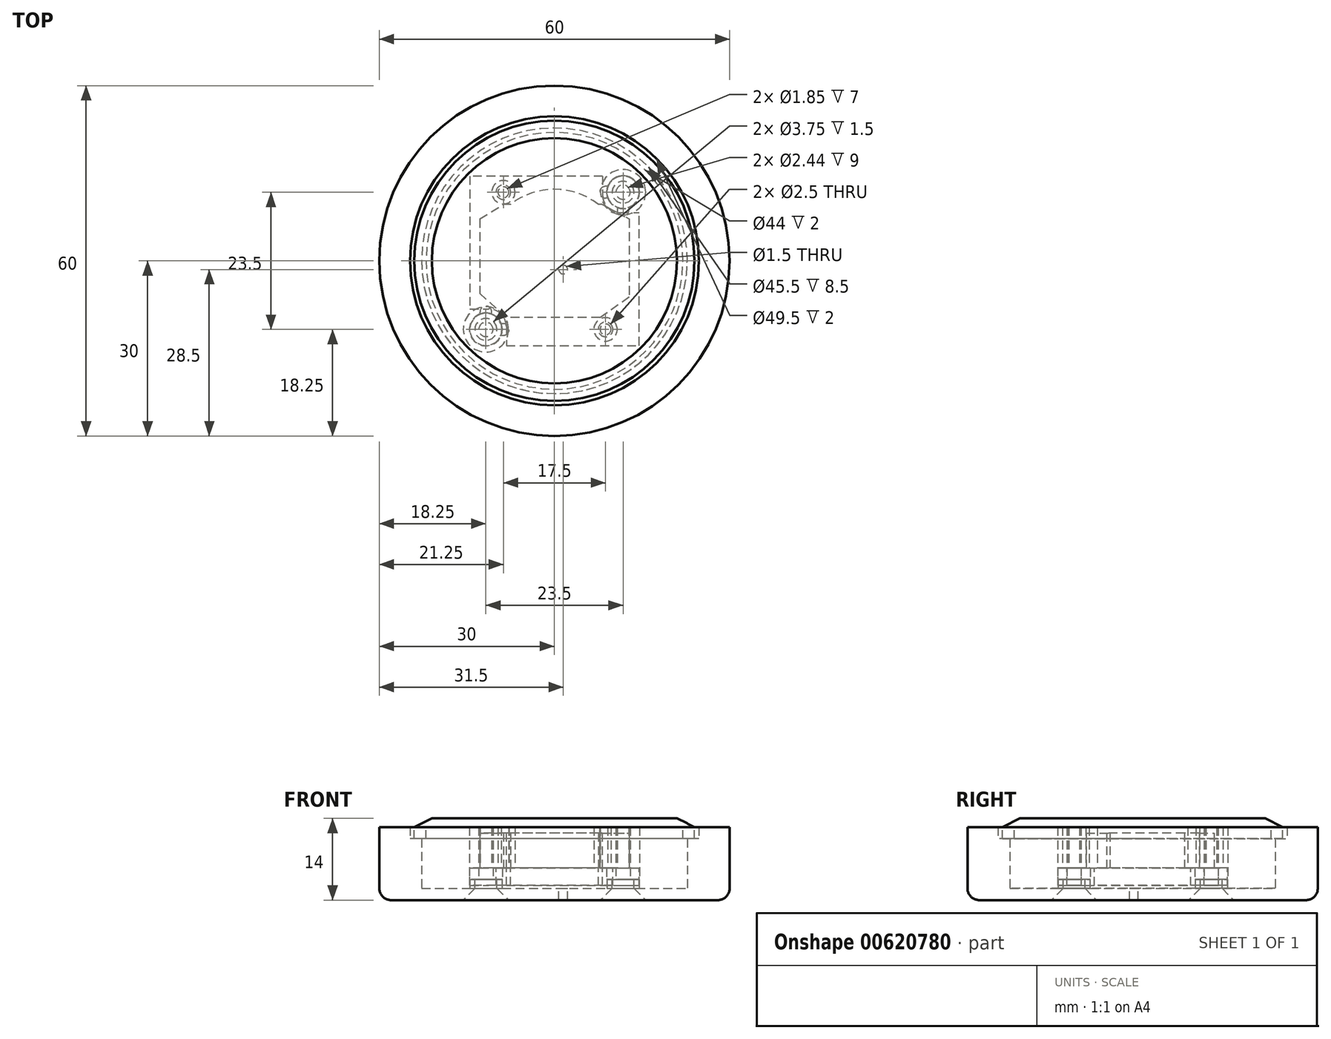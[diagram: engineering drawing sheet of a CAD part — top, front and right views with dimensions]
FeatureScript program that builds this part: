
annotation { "Feature Type Name" : "Feature", "Feature Type Description" : "" }
export const myFeature = defineFeature(function(context is Context, id is Id, definition is map)
    precondition{}
    {
        {
            var Q0;
            Q0=qCreatedBy(makeId("Top.planeOp"),FACE);
            var sketch = newSketch(context, id + "F0", { "sketchPlane" : qUnion([Q0])});
            skPoint(sketch, "E0.middle", {"position": v(0, 0) * mm});
            skCircle(sketch, "E1", {"center": v(-8.75, 11.75) * mm, "radius": 1.25 * mm});
            skLineSegment(sketch, "E2", {"start": v(8.25, 14.5) * mm, "end": v(8.25, 11.25) * mm});
            skLineSegment(sketch, "E3", {"start": v(11.25, 8.25) * mm, "end": v(14.5, 8.25) * mm});
            skLineSegment(sketch, "E4", {"start": v(8.25, 14.5) * mm, "end": v(-14.5, 14.5) * mm});
            skLineSegment(sketch, "E5", {"start": v(14.5, -14.5) * mm, "end": v(14.5, 8.25) * mm});
            skArc(sketch, "E6.filletArc", {"start": v(8.25, 11.25) * mm, "mid": v(9.13, 9.13) * mm, "end": v(11.25, 8.25) * mm});
            skLineSegment(sketch, "E7", {"start": v(-14.5, 14.5) * mm, "end": v(-14.5, -8.25) * mm});
            skLineSegment(sketch, "E8", {"start": v(-14.5, -8.25) * mm, "end": v(-11.25, -8.25) * mm});
            skLineSegment(sketch, "E9", {"start": v(-8.25, -11.25) * mm, "end": v(-8.25, -14.5) * mm});
            skLineSegment(sketch, "E10", {"start": v(-8.25, -14.5) * mm, "end": v(14.5, -14.5) * mm});
            skArc(sketch, "E11.filletArc", {"start": v(-8.25, -11.25) * mm, "mid": v(-9.13, -9.13) * mm, "end": v(-11.25, -8.25) * mm});
            skCircle(sketch, "E12", {"center": v(8.75, -11.75) * mm, "radius": 1.25 * mm});
            skSolve(sketch);
        }
        {
            var Q0;
            Q0=makeQuery(id+"F0.imprint","IMPRINT",FACE,{"disambiguationData":[TD([[makeQuery(id+"F0.imprint","IMPRINT",EDGE,{"derivedFrom":sQuery(id+"F0.wireOp",EDGE,"E1")}),-1.0]])]});
            extrude(context, id + "F1", {"entities" : qUnion([Q0]), "oppositeDirection" : true, "depth" : 3 * mm, "offsetDistance" : 25 * mm});
        }
        {
            var Q0;
            Q0=qCreatedBy(makeId("Top.planeOp"),FACE);
            var sketch = newSketch(context, id + "F2", { "sketchPlane" : qUnion([Q0])});
            skCircle(sketch, "E13", {"center": v(0, 0) * mm, "radius": 12.25 * mm});
            skLineSegment(sketch, "E14.bottom", {"start": v(12.8, 9.68) * mm, "end": v(-12.8, 9.68) * mm});
            skLineSegment(sketch, "E14.top", {"start": v(12.8, -9.68) * mm, "end": v(-12.8, -9.68) * mm});
            skLineSegment(sketch, "E14.left", {"start": v(12.8, 9.68) * mm, "end": v(12.8, -9.68) * mm});
            skLineSegment(sketch, "E14.right", {"start": v(-12.8, 9.68) * mm, "end": v(-12.8, -9.68) * mm});
            skLineSegment(sketch, "E15", {"start": v(8.17, 9.68) * mm, "end": v(12.8, 7.18) * mm});
            skLineSegment(sketch, "E16", {"start": v(7.8, -9.68) * mm, "end": v(12.8, -6.18) * mm});
            skLineSegment(sketch, "E17", {"start": v(-8.3, -9.68) * mm, "end": v(-12.8, -5.58) * mm});
            skLineSegment(sketch, "E18", {"start": v(-12.8, 7.18) * mm, "end": v(-8.71, 9.68) * mm});
            skSolve(sketch);
        }
        {
            var Q0;
            {var subQ0=sQuery(id+"F2.wireOp",EDGE,"E14.bottom");var subQ1=sQuery(id+"F2.wireOp",EDGE,"E13");var subQ2=makeQuery(id+"F2.imprint","INTERSECT",VERTEX,{"disambiguationData":[OD(0.0)],"derivedFrom":[subQ1,subQ0]});Q0=makeQuery(id+"F2.imprint","IMPRINT",FACE,{"disambiguationData":[TD([[makeQuery(id+"F2.imprint","IMPRINT",EDGE,{"disambiguationData":[TD([[subQ2,1.0]])],"derivedFrom":subQ1}),1.0]])]});}
            var Q1;
            {var subQ0=sQuery(id+"F2.wireOp",EDGE,"E14.top");var subQ1=sQuery(id+"F2.wireOp",EDGE,"E13");var subQ2=makeQuery(id+"F2.imprint","INTERSECT",VERTEX,{"disambiguationData":[OD(0.0)],"derivedFrom":[subQ1,subQ0]});Q1=makeQuery(id+"F2.imprint","IMPRINT",FACE,{"disambiguationData":[TD([[makeQuery(id+"F2.imprint","IMPRINT",EDGE,{"disambiguationData":[TD([[subQ2,-1.0]])],"derivedFrom":subQ1}),1.0]])]});}
            var Q2;
            {var subQ0=sQuery(id+"F2.wireOp",EDGE,"E17");Q2=makeQuery(id+"F2.imprint","IMPRINT",FACE,{"disambiguationData":[TD([[makeQuery(id+"F2.imprint","IMPRINT",EDGE,{"derivedFrom":subQ0}),-1.0]])]});}
            var Q3;
            {var subQ0=sQuery(id+"F2.wireOp",EDGE,"E15");Q3=makeQuery(id+"F2.imprint","IMPRINT",FACE,{"disambiguationData":[TD([[makeQuery(id+"F2.imprint","IMPRINT",EDGE,{"derivedFrom":subQ0}),-1.0]])]});}
            var Q4;
            {var subQ0=sQuery(id+"F2.wireOp",EDGE,"E14.bottom");var subQ1=sQuery(id+"F2.wireOp",EDGE,"E13");var subQ2=makeQuery(id+"F2.imprint","INTERSECT",VERTEX,{"disambiguationData":[OD(0.0)],"derivedFrom":[subQ1,subQ0]});Q4=makeQuery(id+"F2.imprint","IMPRINT",FACE,{"disambiguationData":[TD([[makeQuery(id+"F2.imprint","IMPRINT",EDGE,{"disambiguationData":[TD([[subQ2,-1.0]])],"derivedFrom":subQ1}),1.0]])]});}
            extrude(context, id + "F3", {"entities" : qUnion([Q0, Q1, Q2, Q3, Q4]), "operationType" : NewBodyOperationType.ADD, "depth" : 6 * mm, "offsetDistance" : 25 * mm});
        }
        {
            var Q0;
            Q0=qCreatedBy(makeId("Top.planeOp"),FACE);
            var sketch = newSketch(context, id + "F4", { "sketchPlane" : qUnion([Q0])});
            skCircle(sketch, "E19", {"center": v(-11.75, -11.75) * mm, "radius": 1.22 * mm});
            skCircle(sketch, "E20", {"center": v(11.75, 11.75) * mm, "radius": 1.22 * mm});
            skCircle(sketch, "E21", {"center": v(11.75, 11.75) * mm, "radius": 2.81 * mm});
            skCircle(sketch, "E22", {"center": v(-11.75, -11.75) * mm, "radius": 2.81 * mm});
            skLineSegment(sketch, "E23", {"start": v(-8.94, -8.94) * mm, "end": v(8.94, -8.94) * mm, "construction": true});
            skLineSegment(sketch, "E24", {"start": v(8.94, 8.94) * mm, "end": v(-8.94, 8.94) * mm, "construction": true});
            skLineSegment(sketch, "E25", {"start": v(8.94, -8.94) * mm, "end": v(8.94, 8.94) * mm, "construction": true});
            skLineSegment(sketch, "E26", {"start": v(-8.94, 8.94) * mm, "end": v(-8.94, -8.94) * mm, "construction": true});
            skPoint(sketch, "E27", {"position": v(-8.94, 0) * mm});
            skPoint(sketch, "E28", {"position": v(0, 8.94) * mm});
            skPoint(sketch, "E29", {"position": v(8.75, -11.75) * mm});
            skCircle(sketch, "E30", {"center": v(-8.75, 11.75) * mm, "radius": 2 * mm});
            skCircle(sketch, "E31", {"center": v(8.75, -11.75) * mm, "radius": 2 * mm});
            skCircle(sketch, "E32", {"center": v(-8.75, 11.75) * mm, "radius": 0.93 * mm});
            skCircle(sketch, "E33", {"center": v(8.75, -11.75) * mm, "radius": 0.93 * mm});
            skLineSegment(sketch, "E34", {"start": v(-11.75, -11.75) * mm, "end": v(-11.75, -7.75) * mm, "construction": true});
            skLineSegment(sketch, "E35", {"start": v(-8.94, 8.94) * mm, "end": v(8.94, -8.94) * mm, "construction": true});
            skLineSegment(sketch, "E36", {"start": v(-11.75, -7.75) * mm, "end": v(-11.75, -7.75) * mm});
            skLineSegment(sketch, "E37", {"start": v(-12.75, -9.12) * mm, "end": v(-12.75, -8.75) * mm});
            skPoint(sketch, "E38.visualSharp", {"position": v(-12.75, -7.75) * mm});
            skArc(sketch, "E38.filletArc", {"start": v(-11.75, -7.75) * mm, "mid": v(-12.46, -8.04) * mm, "end": v(-12.75, -8.75) * mm});
            skArc(sketch, "E39.MirrorCS", {"start": v(-11.75, -7.75) * mm, "mid": v(-11.04, -8.04) * mm, "end": v(-10.75, -8.75) * mm});
            skLineSegment(sketch, "E40.MirrorCS", {"start": v(-10.75, -9.12) * mm, "end": v(-10.75, -8.75) * mm});
            skLineSegment(sketch, "E41", {"start": v(8.94, 8.94) * mm, "end": v(-8.94, -8.94) * mm, "construction": true});
            skLineSegment(sketch, "E42.MirrorCS", {"start": v(-9.12, -12.75) * mm, "end": v(-8.75, -12.75) * mm});
            skArc(sketch, "E43.MirrorCS", {"start": v(-7.75, -11.75) * mm, "mid": v(-8.04, -12.46) * mm, "end": v(-8.75, -12.75) * mm});
            skArc(sketch, "E44.MirrorCS", {"start": v(-7.75, -11.75) * mm, "mid": v(-8.04, -11.04) * mm, "end": v(-8.75, -10.75) * mm});
            skLineSegment(sketch, "E45.MirrorCS", {"start": v(-9.12, -10.75) * mm, "end": v(-8.75, -10.75) * mm});
            skLineSegment(sketch, "E46.MirrorCS", {"start": v(10.75, 9.12) * mm, "end": v(10.75, 8.75) * mm});
            skArc(sketch, "E47.MirrorCS", {"start": v(11.75, 7.75) * mm, "mid": v(11.04, 8.04) * mm, "end": v(10.75, 8.75) * mm});
            skArc(sketch, "E48.MirrorCS", {"start": v(11.75, 7.75) * mm, "mid": v(12.46, 8.04) * mm, "end": v(12.75, 8.75) * mm});
            skLineSegment(sketch, "E49.MirrorCS", {"start": v(12.75, 9.12) * mm, "end": v(12.75, 8.75) * mm});
            skLineSegment(sketch, "E50.MirrorCS", {"start": v(9.12, 10.75) * mm, "end": v(8.75, 10.75) * mm});
            skArc(sketch, "E51.MirrorCS", {"start": v(7.75, 11.75) * mm, "mid": v(8.04, 11.04) * mm, "end": v(8.75, 10.75) * mm});
            skArc(sketch, "E52.MirrorCS", {"start": v(7.75, 11.75) * mm, "mid": v(8.04, 12.46) * mm, "end": v(8.75, 12.75) * mm});
            skLineSegment(sketch, "E53.MirrorCS", {"start": v(9.12, 12.75) * mm, "end": v(8.75, 12.75) * mm});
            skCircle(sketch, "E54", {"center": v(0, 0) * mm, "radius": 30 * mm, "construction": true});
            skCircle(sketch, "E55", {"center": v(1.5, -1.5) * mm, "radius": 0.75 * mm});
            skLineSegment(sketch, "E56", {"start": v(-11.75, -11.75) * mm, "end": v(1.5, -1.5) * mm, "construction": true});
            skLineSegment(sketch, "E57", {"start": v(-8.75, 11.75) * mm, "end": v(1.5, -1.5) * mm, "construction": true});
            skSolve(sketch);
        }
        {
            var Q0;
            Q0=makeQuery(id+"F4.imprint","IMPRINT",FACE,{"disambiguationData":[TD([[makeQuery(id+"F4.imprint","IMPRINT",EDGE,{"derivedFrom":sQuery(id+"F4.wireOp",EDGE,"E19")}),-1.0]])]});
            var Q1;
            Q1=makeQuery(id+"F4.imprint","IMPRINT",FACE,{"disambiguationData":[TD([[makeQuery(id+"F4.imprint","IMPRINT",EDGE,{"derivedFrom":sQuery(id+"F4.wireOp",EDGE,"E31")}),1.0]])]});
            var Q2;
            {var subQ0=sQuery(id+"F4.wireOp",EDGE,"E42.MirrorCS");Q2=makeQuery(id+"F4.imprint","IMPRINT",FACE,{"disambiguationData":[TD([[makeQuery(id+"F4.imprint","IMPRINT",EDGE,{"derivedFrom":subQ0}),1.0]])]});}
            var Q3;
            {var subQ0=sQuery(id+"F4.wireOp",EDGE,"E50.MirrorCS");Q3=makeQuery(id+"F4.imprint","IMPRINT",FACE,{"disambiguationData":[TD([[makeQuery(id+"F4.imprint","IMPRINT",EDGE,{"derivedFrom":subQ0}),-1.0]])]});}
            var Q4;
            {var subQ0=sQuery(id+"F4.wireOp",EDGE,"E46.MirrorCS");Q4=makeQuery(id+"F4.imprint","IMPRINT",FACE,{"disambiguationData":[TD([[makeQuery(id+"F4.imprint","IMPRINT",EDGE,{"derivedFrom":subQ0}),1.0]])]});}
            var Q5;
            Q5=makeQuery(id+"F4.imprint","IMPRINT",FACE,{"disambiguationData":[TD([[makeQuery(id+"F4.imprint","IMPRINT",EDGE,{"derivedFrom":sQuery(id+"F4.wireOp",EDGE,"E20")}),-1.0]])]});
            var Q6;
            Q6=makeQuery(id+"F4.imprint","IMPRINT",FACE,{"disambiguationData":[TD([[makeQuery(id+"F4.imprint","IMPRINT",EDGE,{"derivedFrom":sQuery(id+"F4.wireOp",EDGE,"E30")}),1.0]])]});
            var Q7;
            {var subQ0=sQuery(id+"F4.wireOp",EDGE,"E37");Q7=makeQuery(id+"F4.imprint","IMPRINT",FACE,{"disambiguationData":[TD([[makeQuery(id+"F4.imprint","IMPRINT",EDGE,{"derivedFrom":subQ0}),-1.0]])]});}
            extrude(context, id + "F5", {"entities" : qUnion([Q0, Q1, Q2, Q3, Q4, Q5, Q6, Q7]), "depth" : 7 * mm, "offsetDistance" : 25 * mm});
        }
        {
            var Q0;
            Q0=makeQuery(id+"F5.opExtrude","CAP_FACE",FACE,{"disambiguationData":[OSD([sQuery(id+"F4.wireOp",EDGE,"E19"),sQuery(id+"F4.wireOp",EDGE,"E22"),sQuery(id+"F4.wireOp",EDGE,"E37"),sQuery(id+"F4.wireOp",EDGE,"E38.filletArc"),sQuery(id+"F4.wireOp",EDGE,"E39.MirrorCS"),sQuery(id+"F4.wireOp",EDGE,"E40.MirrorCS"),sQuery(id+"F4.wireOp",EDGE,"E42.MirrorCS"),sQuery(id+"F4.wireOp",EDGE,"E43.MirrorCS"),sQuery(id+"F4.wireOp",EDGE,"E44.MirrorCS"),sQuery(id+"F4.wireOp",EDGE,"E45.MirrorCS")])],"isStart":false});
            cPlane(context, id + "F6", {"entities" : qUnion([Q0]), "cplaneType" : CPlaneType.OFFSET, "offset" : 0 * mm, "width" : 150 * mm, "height" : 150 * mm});
        }
        {
            var Q0;
            Q0=qCreatedBy(id+"F6.planeOp",FACE);
            var sketch = newSketch(context, id + "F7", { "sketchPlane" : qUnion([Q0])});
            skPoint(sketch, "E58", {"position": v(0, 0) * mm});
            skCircle(sketch, "E59", {"center": v(0, 0) * mm, "radius": 24 * mm});
            skCircle(sketch, "E60", {"center": v(0, 0) * mm, "radius": 21 * mm});
            skCircle(sketch, "E61", {"center": v(0, 0) * mm, "radius": 22 * mm});
            skSolve(sketch);
        }
        {
            var Q0;
            Q0=qSketchRegion(id+"F7",true);
            var Q1;
            Q1=makeQuery(id+"F7.imprint","IMPRINT",FACE,{"disambiguationData":[TD([[makeQuery(id+"F7.imprint","IMPRINT",EDGE,{"derivedFrom":sQuery(id+"F7.wireOp",EDGE,"E60")}),1.0]])]});
            var Q2;
            Q2=makeQuery(id+"F7.imprint","IMPRINT",FACE,{"disambiguationData":[TD([[makeQuery(id+"F7.imprint","IMPRINT",EDGE,{"derivedFrom":sQuery(id+"F7.wireOp",EDGE,"E60")}),-1.0]])]});
            extrude(context, id + "F8", {"entities" : qUnion([Q0, Q1, Q2]), "operationType" : NewBodyOperationType.ADD, "depth" : 1.5 * mm, "offsetDistance" : 25 * mm});
        }
        {
            var Q0;
            Q0=makeQuery(id+"F4.imprint","IMPRINT",FACE,{"disambiguationData":[TD([[makeQuery(id+"F4.imprint","IMPRINT",EDGE,{"derivedFrom":sQuery(id+"F4.wireOp",EDGE,"E19")}),-1.0]])]});
            var Q1;
            Q1=makeQuery(id+"F4.imprint","IMPRINT",FACE,{"disambiguationData":[TD([[makeQuery(id+"F4.imprint","IMPRINT",EDGE,{"derivedFrom":sQuery(id+"F4.wireOp",EDGE,"E20")}),-1.0]])]});
            extrude(context, id + "F9", {"entities" : qUnion([Q0, Q1]), "operationType" : NewBodyOperationType.ADD, "oppositeDirection" : true, "depth" : 2 * mm, "offsetDistance" : 25 * mm});
        }
        {
            var Q0;
            Q0=qCreatedBy(makeId("Front.planeOp"),FACE);
            var sketch = newSketch(context, id + "F10", { "sketchPlane" : qUnion([Q0])});
            skLineSegment(sketch, "E62", {"start": v(-21, 7) * mm, "end": v(-24, 7) * mm, "construction": true});
            skLineSegment(sketch, "E63", {"start": v(-24, 7) * mm, "end": v(-24, 8.5) * mm});
            skLineSegment(sketch, "E64", {"start": v(-24, 8.5) * mm, "end": v(-21, 8.5) * mm});
            skLineSegment(sketch, "E65", {"start": v(-21, 8.5) * mm, "end": v(-24, 7) * mm});
            skLineSegment(sketch, "E66", {"start": v(0, -26.12) * mm, "end": v(0, 34.53) * mm, "construction": true});
            skSolve(sketch);
        }
        {
            var Q0;
            Q0=qSketchRegion(id+"F10",true);
            var Q1;
            Q1=sQuery(id+"F10.wireOp",EDGE,"E66");
            revolve(context, id + "F11", {"operationType" : NewBodyOperationType.REMOVE, "entities" : qUnion([Q0]), "axis" : qUnion([Q1]), "revolveType" : RevolveType.FULL, "oppositeDirection" : true});
        }
        {
            var Q0;
            Q0=makeQuery(id+"F7.imprint","IMPRINT",FACE,{"disambiguationData":[TD([[makeQuery(id+"F7.imprint","IMPRINT",EDGE,{"derivedFrom":sQuery(id+"F7.wireOp",EDGE,"E59")}),1.0]])]});
            extrude(context, id + "F12", {"entities" : qUnion([Q0]), "operationType" : NewBodyOperationType.ADD, "oppositeDirection" : true, "depth" : 2 * mm, "offsetDistance" : 25 * mm});
        }
        {
            var Q0;
            Q0=makeQuery(id+"F1.opExtrude","CAP_FACE",FACE,{"disambiguationData":[OSD([sQuery(id+"F0.wireOp",EDGE,"E1"),sQuery(id+"F0.wireOp",EDGE,"E2"),sQuery(id+"F0.wireOp",EDGE,"E3"),sQuery(id+"F0.wireOp",EDGE,"E4"),sQuery(id+"F0.wireOp",EDGE,"E5"),sQuery(id+"F0.wireOp",EDGE,"E6.filletArc"),sQuery(id+"F0.wireOp",EDGE,"E7"),sQuery(id+"F0.wireOp",EDGE,"E8"),sQuery(id+"F0.wireOp",EDGE,"E9"),sQuery(id+"F0.wireOp",EDGE,"E10"),sQuery(id+"F0.wireOp",EDGE,"E11.filletArc"),sQuery(id+"F0.wireOp",EDGE,"E12")])],"isStart":false});
            cPlane(context, id + "F13", {"entities" : qUnion([Q0]), "cplaneType" : CPlaneType.OFFSET, "offset" : 0.5 * mm, "width" : 150 * mm, "height" : 150 * mm});
        }
        {
            var Q0;
            Q0=qCreatedBy(id+"F13.planeOp",FACE);
            var sketch = newSketch(context, id + "F14", { "sketchPlane" : qUnion([Q0])});
            skPoint(sketch, "E67", {"position": v(-11.75, 11.75) * mm});
            skPoint(sketch, "E68", {"position": v(0, 0) * mm});
            skPoint(sketch, "E69", {"position": v(11.75, -11.75) * mm});
            skCircle(sketch, "E70", {"center": v(-11.75, 11.75) * mm, "radius": 1.88 * mm});
            skCircle(sketch, "E71", {"center": v(-11.75, 11.75) * mm, "radius": 2.75 * mm});
            skCircle(sketch, "E72", {"center": v(11.75, -11.75) * mm, "radius": 1.88 * mm});
            skCircle(sketch, "E73", {"center": v(11.75, -11.75) * mm, "radius": 2.75 * mm});
            skPoint(sketch, "E74", {"position": v(1.5, 1.5) * mm});
            skCircle(sketch, "E75", {"center": v(1.5, 1.5) * mm, "radius": 0.75 * mm});
            skCircle(sketch, "E76", {"center": v(0, 0) * mm, "radius": 24 * mm, "construction": true});
            skCircle(sketch, "E77", {"center": v(0, 0) * mm, "radius": 22.75 * mm});
            skCircle(sketch, "E78", {"center": v(0, 0) * mm, "radius": 24.75 * mm});
            skCircle(sketch, "E79", {"center": v(0, 0) * mm, "radius": 30 * mm});
            skSolve(sketch);
        }
        {
            var Q0;
            Q0=makeQuery(id+"F14.imprint","IMPRINT",FACE,{"disambiguationData":[TD([[makeQuery(id+"F14.imprint","IMPRINT",EDGE,{"derivedFrom":sQuery(id+"F14.wireOp",EDGE,"E78")}),-1.0]])]});
            var Q1;
            Q1=makeQuery(id+"F14.imprint","IMPRINT",FACE,{"disambiguationData":[TD([[makeQuery(id+"F14.imprint","IMPRINT",EDGE,{"derivedFrom":sQuery(id+"F14.wireOp",EDGE,"E77")}),-1.0]])]});
            var Q2;
            Q2=makeQuery(id+"F14.imprint","IMPRINT",FACE,{"disambiguationData":[TD([[makeQuery(id+"F14.imprint","IMPRINT",EDGE,{"derivedFrom":sQuery(id+"F14.wireOp",EDGE,"E71")}),-1.0]])]});
            var Q3;
            Q3=makeQuery(id+"F14.imprint","IMPRINT",FACE,{"disambiguationData":[TD([[makeQuery(id+"F14.imprint","IMPRINT",EDGE,{"derivedFrom":sQuery(id+"F14.wireOp",EDGE,"E70")}),-1.0]])]});
            var Q4;
            Q4=makeQuery(id+"F14.imprint","IMPRINT",FACE,{"disambiguationData":[TD([[makeQuery(id+"F14.imprint","IMPRINT",EDGE,{"derivedFrom":sQuery(id+"F14.wireOp",EDGE,"E72")}),-1.0]])]});
            extrude(context, id + "F15", {"entities" : qUnion([Q0, Q1, Q2, Q3, Q4]), "depth" : 2 * mm, "offsetDistance" : 25 * mm});
        }
        {
            var Q0;
            Q0=makeQuery(id+"F14.imprint","IMPRINT",FACE,{"disambiguationData":[TD([[makeQuery(id+"F14.imprint","IMPRINT",EDGE,{"derivedFrom":sQuery(id+"F14.wireOp",EDGE,"E72")}),-1.0]])]});
            var Q1;
            Q1=makeQuery(id+"F14.imprint","IMPRINT",FACE,{"disambiguationData":[TD([[makeQuery(id+"F14.imprint","IMPRINT",EDGE,{"derivedFrom":sQuery(id+"F14.wireOp",EDGE,"E70")}),-1.0]])]});
            extrude(context, id + "F16", {"entities" : qUnion([Q0, Q1]), "operationType" : NewBodyOperationType.ADD, "oppositeDirection" : true, "depth" : 1.5 * mm, "offsetDistance" : 25 * mm});
        }
        {
            var Q0;
            Q0=makeQuery(id+"F15.opExtrude","CAP_EDGE",EDGE,{"disambiguationData":[OSD([sQuery(id+"F14.wireOp",EDGE,"E70")])],"isStart":false});
            var Q1;
            Q1=makeQuery(id+"F15.opExtrude","CAP_EDGE",EDGE,{"disambiguationData":[OSD([sQuery(id+"F14.wireOp",EDGE,"E72")])],"isStart":false});
            chamfer(context, id + "F17", {"entities" : qUnion([Q0, Q1]), "width" : 2 * mm, "tangentPropagation" : true});
        }
        {
            var Q0;
            Q0=makeQuery(id+"F14.imprint","IMPRINT",FACE,{"disambiguationData":[TD([[makeQuery(id+"F14.imprint","IMPRINT",EDGE,{"derivedFrom":sQuery(id+"F14.wireOp",EDGE,"E77")}),-1.0]])]});
            var Q1;
            Q1=makeQuery(id+"F12.opExtrude","CAP_FACE",FACE,{"disambiguationData":[OSD([sQuery(id+"F7.wireOp",EDGE,"E59"),sQuery(id+"F7.wireOp",EDGE,"E61")])],"isStart":false});
            extrude(context, id + "F18", {"entities" : qUnion([Q0]), "operationType" : NewBodyOperationType.ADD, "endBound" : BoundingType.UP_TO_SURFACE, "oppositeDirection" : true, "depth" : 25 * mm, "endBoundEntityFace" : qUnion([Q1]), "offsetDistance" : 25 * mm});
        }
        {
            var Q0;
            Q0=makeQuery(id+"F14.imprint","IMPRINT",FACE,{"disambiguationData":[TD([[makeQuery(id+"F14.imprint","IMPRINT",EDGE,{"derivedFrom":sQuery(id+"F14.wireOp",EDGE,"E78")}),-1.0]])]});
            extrude(context, id + "F19", {"entities" : qUnion([Q0]), "operationType" : NewBodyOperationType.ADD, "oppositeDirection" : true, "depth" : 10.5 * mm, "offsetDistance" : 25 * mm});
        }
        {
            var Q0;
            Q0=makeQuery(id+"F15.opExtrude","CAP_EDGE",EDGE,{"disambiguationData":[OSD([sQuery(id+"F14.wireOp",EDGE,"E79")])],"isStart":false});
            fillet(context, id + "F20", {"entities" : qUnion([Q0]), "radius" : 2 * mm, "tangentPropagation" : true, "allowEdgeOverflow" : false});
        }
    });
